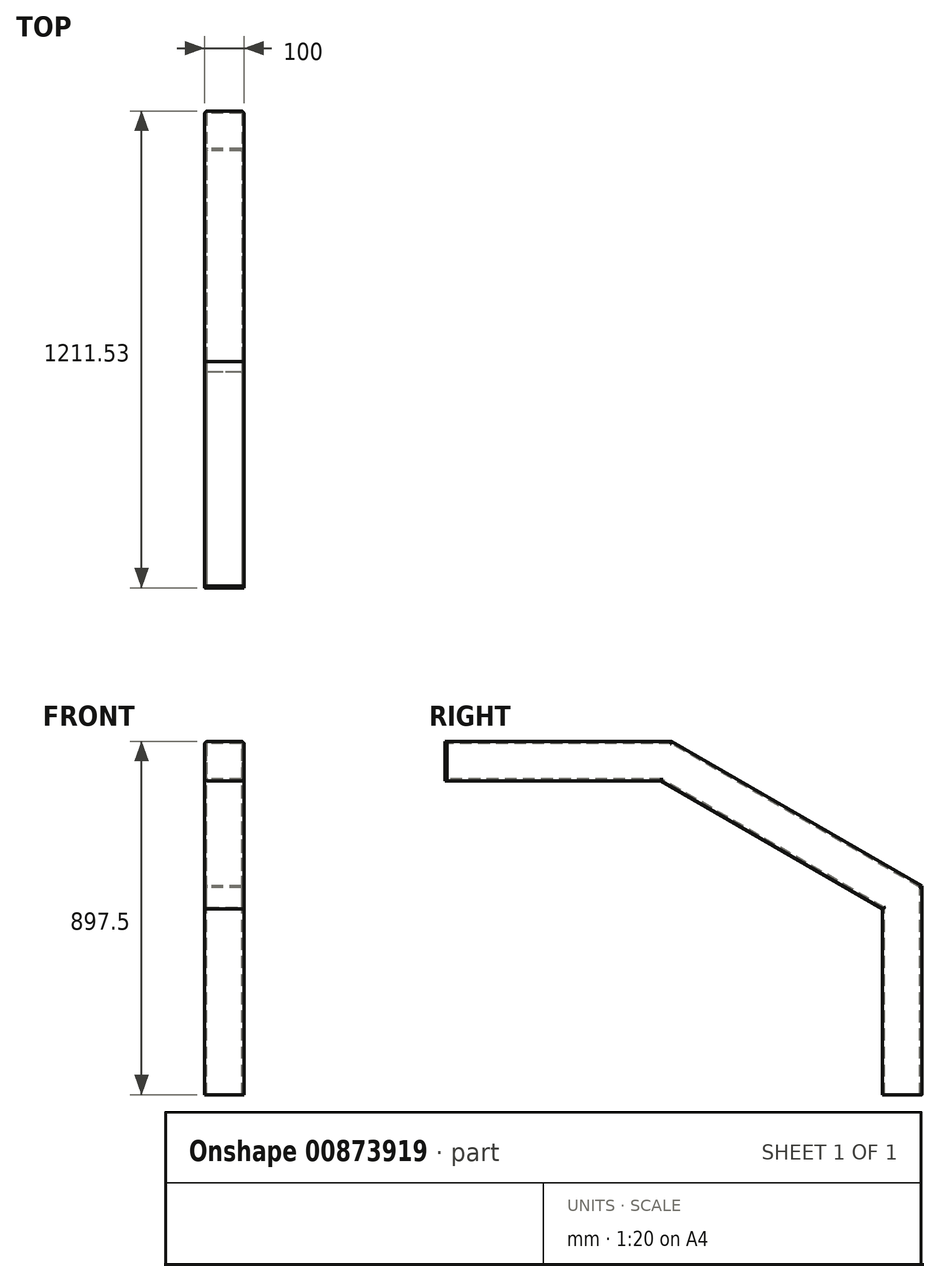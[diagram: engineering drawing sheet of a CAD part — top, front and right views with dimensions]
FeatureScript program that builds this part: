
annotation { "Feature Type Name" : "Feature", "Feature Type Description" : "" }
export const myFeature = defineFeature(function(context is Context, id is Id, definition is map)
    precondition{}
    {
        {
            var Q0;
            Q0=qCreatedBy(makeId("Top.planeOp"),FACE);
            var sketch = newSketch(context, id + "F0", { "sketchPlane" : qUnion([Q0])});
            skLineSegment(sketch, "E0.bottom", {"start": v(43, 50) * mm, "end": v(-43, 50) * mm});
            skLineSegment(sketch, "E0.top", {"start": v(43, -50) * mm, "end": v(-43, -50) * mm});
            skLineSegment(sketch, "E0.left", {"start": v(50, 43) * mm, "end": v(50, -43) * mm});
            skLineSegment(sketch, "E0.right", {"start": v(-50, 43) * mm, "end": v(-50, -43) * mm});
            skPoint(sketch, "E0.middle", {"position": v(0, 0) * mm});
            skPoint(sketch, "E1.visualSharp", {"position": v(-50, 50) * mm});
            skArc(sketch, "E1.filletArc", {"start": v(-43, 50) * mm, "mid": v(-47.95, 47.95) * mm, "end": v(-50, 43) * mm});
            skPoint(sketch, "E2.visualSharp", {"position": v(-50, -50) * mm});
            skArc(sketch, "E2.filletArc", {"start": v(-50, -43) * mm, "mid": v(-47.95, -47.95) * mm, "end": v(-43, -50) * mm});
            skPoint(sketch, "E3.visualSharp", {"position": v(50, 50) * mm});
            skArc(sketch, "E3.filletArc", {"start": v(50, 43) * mm, "mid": v(47.95, 47.95) * mm, "end": v(43, 50) * mm});
            skPoint(sketch, "E4.visualSharp", {"position": v(50, -50) * mm});
            skArc(sketch, "E4.filletArc", {"start": v(43, -50) * mm, "mid": v(47.95, -47.95) * mm, "end": v(50, -43) * mm});
            skArc(sketch, "E5.0", {"start": v(43, -45) * mm, "mid": v(44.41, -44.41) * mm, "end": v(45, -43) * mm});
            skLineSegment(sketch, "E5.1", {"start": v(45, 43) * mm, "end": v(45, -43) * mm});
            skLineSegment(sketch, "E5.2", {"start": v(43, -45) * mm, "end": v(-43, -45) * mm});
            skArc(sketch, "E5.3", {"start": v(45, 43) * mm, "mid": v(44.41, 44.41) * mm, "end": v(43, 45) * mm});
            skArc(sketch, "E5.4", {"start": v(-45, -43) * mm, "mid": v(-44.41, -44.41) * mm, "end": v(-43, -45) * mm});
            skLineSegment(sketch, "E5.5", {"start": v(-45, 43) * mm, "end": v(-45, -43) * mm});
            skArc(sketch, "E5.6", {"start": v(-43, 45) * mm, "mid": v(-44.41, 44.41) * mm, "end": v(-45, 43) * mm});
            skLineSegment(sketch, "E5.7", {"start": v(43, 45) * mm, "end": v(-43, 45) * mm});
            skSolve(sketch);
        }
        {
            var Q0;
            Q0=qCreatedBy(makeId("Right.planeOp"),FACE);
            var sketch = newSketch(context, id + "F1", { "sketchPlane" : qUnion([Q0])});
            skLineSegment(sketch, "E6", {"start": v(0, 0) * mm, "end": v(50, 0) * mm, "construction": true});
            skLineSegment(sketch, "E7", {"start": v(50, 0) * mm, "end": v(50, 530) * mm});
            skLineSegment(sketch, "E8", {"start": v(50, 530) * mm, "end": v(-586.53, 897.5) * mm});
            skLineSegment(sketch, "E9", {"start": v(-586.53, 897.5) * mm, "end": v(-1156.53, 897.5) * mm});
            skSolve(sketch);
        }
        {
            var Q0;
            Q0=makeQuery(id+"F0.imprint","IMPRINT",FACE,{"disambiguationData":[TD([[makeQuery(id+"F0.imprint","IMPRINT",EDGE,{"derivedFrom":sQuery(id+"F0.wireOp",EDGE,"E0.bottom")}),1.0]])]});
            var Q1;
            Q1 = qConstructionFilter(qBodyType(qCreatedBy(id + "F1" ,EDGE), BodyType.WIRE), ConstructionObject.NO);
            sweep(context, id + "F2", {"profiles" : qUnion([Q0]), "path" : qUnion([Q1])});
        }
        {
            var Q0;
            Q0=makeQuery(id+"F2.opSweep","CAP_FACE",FACE,{"disambiguationData":[OSD([sQuery(id+"F0.wireOp",EDGE,"E0.bottom"),sQuery(id+"F0.wireOp",EDGE,"E0.top"),sQuery(id+"F0.wireOp",EDGE,"E0.left"),sQuery(id+"F0.wireOp",EDGE,"E0.right"),sQuery(id+"F0.wireOp",EDGE,"E1.filletArc"),sQuery(id+"F0.wireOp",EDGE,"E2.filletArc"),sQuery(id+"F0.wireOp",EDGE,"E3.filletArc"),sQuery(id+"F0.wireOp",EDGE,"E4.filletArc"),sQuery(id+"F0.wireOp",EDGE,"E5.0"),sQuery(id+"F0.wireOp",EDGE,"E5.1"),sQuery(id+"F0.wireOp",EDGE,"E5.2"),sQuery(id+"F0.wireOp",EDGE,"E5.3"),sQuery(id+"F0.wireOp",EDGE,"E5.4"),sQuery(id+"F0.wireOp",EDGE,"E5.5"),sQuery(id+"F0.wireOp",EDGE,"E5.6"),sQuery(id+"F0.wireOp",EDGE,"E5.7"),sQuery(id+"F1.wireOp",VERTEX,"E9.end")])],"isStart":false});
            var sketch = newSketch(context, id + "F3", { "sketchPlane" : qUnion([Q0])});
            skLineSegment(sketch, "E10.bottom", {"start": v(43, 897.5) * mm, "end": v(-43, 897.5) * mm});
            skLineSegment(sketch, "E10.top", {"start": v(43, 797.5) * mm, "end": v(-43, 797.5) * mm});
            skLineSegment(sketch, "E10.left", {"start": v(50, 890.5) * mm, "end": v(50, 804.5) * mm});
            skLineSegment(sketch, "E10.right", {"start": v(-50, 890.5) * mm, "end": v(-50, 804.5) * mm});
            skPoint(sketch, "E10.middle", {"position": v(0, 847.5) * mm});
            skPoint(sketch, "E10.middle.positionSnap0", {"position": v(-45, 847.5) * mm});
            skPoint(sketch, "E10.centerSnap0", {"position": v(-45, 847.5) * mm});
            skPoint(sketch, "E11.visualSharp", {"position": v(-50, 897.5) * mm});
            skArc(sketch, "E11.filletArc", {"start": v(-43, 897.5) * mm, "mid": v(-47.95, 895.45) * mm, "end": v(-50, 890.5) * mm});
            skPoint(sketch, "E12.visualSharp", {"position": v(50, 897.5) * mm});
            skArc(sketch, "E12.filletArc", {"start": v(50, 890.5) * mm, "mid": v(47.95, 895.45) * mm, "end": v(43, 897.5) * mm});
            skPoint(sketch, "E13.visualSharp", {"position": v(50, 797.5) * mm});
            skArc(sketch, "E13.filletArc", {"start": v(43, 797.5) * mm, "mid": v(47.95, 799.55) * mm, "end": v(50, 804.5) * mm});
            skPoint(sketch, "E14.visualSharp", {"position": v(-50, 797.5) * mm});
            skArc(sketch, "E14.filletArc", {"start": v(-50, 804.5) * mm, "mid": v(-47.95, 799.55) * mm, "end": v(-43, 797.5) * mm});
            skSolve(sketch);
        }
        {
            var Q0;
            Q0 = qSketchRegion(id + "F3", true);
            extrude(context, id + "F4", {"entities" : qUnion([Q0]), "depth" : 5 * mm, "offsetDistance" : 25 * mm});
        }
    });
